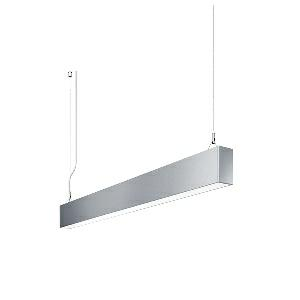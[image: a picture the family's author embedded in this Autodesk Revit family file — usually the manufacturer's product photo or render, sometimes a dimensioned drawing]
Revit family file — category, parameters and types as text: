
# Revit family: idoo_line_-_ilp_3000_vtl_d_00806464_d314
name_source: partatom
category: Lighting Fixtures
units: mm (PartAtom-declared; Revit-internal decimal feet)

## family parameters
Cut with Voids When Loaded = No
Host = Face
Light Source = No
Part Type = Normal
Room Calculation Point = No
Round Connector Dimension = Use Diameter
Shared = No

## types (1)
- IDOO.line - ILP 3000/VTL/D (1 x LED, 3150 lm, 2700-6500K)
    Apparent Load = 32 VA
    Approval mark = CE
    CIE Flux Codes = 66 91 98 40 100
    Color Rendering = 90-100
    Color Temperature = 2700-6500K
    Control Gear = Electronic ballast
    Default Elevation = 1800 mm
    Description = ILP 3000/VTL/D|Suspended luminaire|light source: LED|connected load: 220-240 V, 50/60 Hz|Power consumption: approx. 32 W|standby: approx. 0,25|luminous flux: 3150 lm|luminous efficacy: 98 lm/W|light distribution: Direct/indirect|direct ratio: approx. 40 %|colour temperature: Cold white, ca. 2700-6500 K|color rendering index (CRI): >= 90|chromaticity tolerance:  3 SDCM|System of protection: IP 40|technology: Continuously dimmable|luminaire body|material: Sectional aluminium|colour: Silver|lamp cover: Acrylic (PMMA), Clear|mains lead: 2.00 m With free stranded wires|Fastening: Steel cable 0.3 - 0.7 m|glare control: Prism aperture|luminance(L65): <= 2700 cd/m|unified glare rating(4H 8H): <=  16|special features: Specified values at approx. 4000 K, DALI Load 1x, External control required for Dali Device type 8, Flicker-free, Constant luminous flux between 2700 and 6500 K, Constant colour temperature over the whole dimming range, Suitable as emergency lighting|
    Frequency = 50 Hz
    Height = 110 mm
    Lamp = 1 x LED
    Lamp Light Flux = 3150 lm
    Lamp count = 1
    Length = 1134 mm
    Luminous efficacy = 98 lm/W
    Manufacturer = Waldmann
    ModVariant = No
    Model = 00806464
    Mounting Place = Ceiling
    Mounting Type = Pendant
    Number of Poles = 1
    OnlyDefault = Yes
    Power Factor = 1
    Product Name = IDOO.line - ILP 3000/VTL/D
    Product group = Suspended luminaire
    ProductGroupID = 9
    Protection Class = Protection class I
    Protection Degree = IP 40
    RLX_Detail_Level = 1
    RLX_Emergency_Light_Flux = 0 lm
    RLX_Emergency_Type = 0
    RLX_Emergency_Type_DB = No
    RlxData = <blob elided: 21253 chars, md5=918ac89f>
    Socket = socket
    Standby Power = 0 W
    System Light Flux = 3150 lm
    System Power = 32 W
    Type Comments = Product without accessories
    Type Image = 113290000-00692519.jpg
    URL = http://relux.com
    VarID = ---
    Voltage = 230 V
    Voltage Range = 220-240 V
    Weight = 0.00 kg
    Width = 60 mm  [stored 0.19685 ft]

note: [stored X ft] marks values corroborated as IEEE doubles in the binary element streams (Revit-internal decimal feet)

## geometry (parser evidence)
native form markers: Blend x4, Sweep x14
no freeform markers — native parametric forms only
